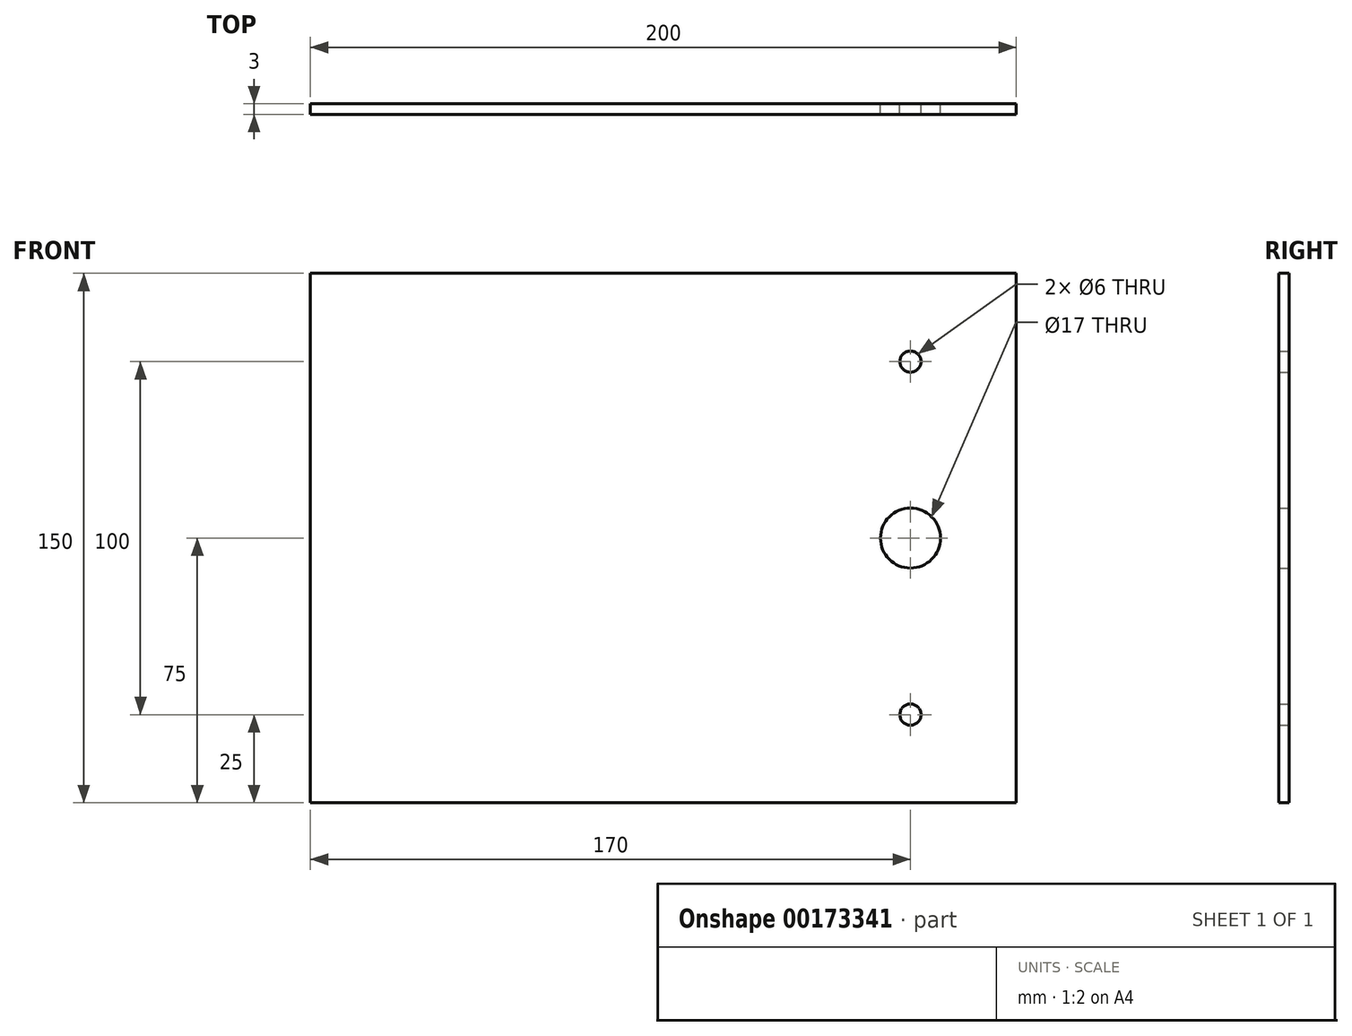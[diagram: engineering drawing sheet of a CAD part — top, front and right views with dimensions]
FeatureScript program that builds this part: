
annotation { "Feature Type Name" : "Feature", "Feature Type Description" : "" }
export const myFeature = defineFeature(function(context is Context, id is Id, definition is map)
    precondition{}
    {
        {
            var Q0;
            Q0=qCreatedBy(makeId("Front.planeOp"),FACE);
            var sketch = newSketch(context, id + "F0", { "sketchPlane" : qUnion([Q0])});
            skLineSegment(sketch, "E0.bottom", {"start": v(-100, 75) * mm, "end": v(100, 75) * mm});
            skLineSegment(sketch, "E0.top", {"start": v(-100, -75) * mm, "end": v(100, -75) * mm});
            skLineSegment(sketch, "E0.left", {"start": v(-100, 75) * mm, "end": v(-100, -75) * mm});
            skLineSegment(sketch, "E0.right", {"start": v(100, 75) * mm, "end": v(100, -75) * mm});
            skCircle(sketch, "E1", {"center": v(70, 0) * mm, "radius": 8.5 * mm});
            skCircle(sketch, "E2", {"center": v(70, 50) * mm, "radius": 3 * mm});
            skCircle(sketch, "E3.MirrorC", {"center": v(70, -50) * mm, "radius": 3 * mm});
            skSolve(sketch);
        }
        {
            var Q0;
            Q0 = qSketchRegion(id + "F0", true);
            extrude(context, id + "F1", {"entities" : qUnion([Q0]), "endBound" : BoundingType.SYMMETRIC, "depth" : 3 * mm});
        }
    });
